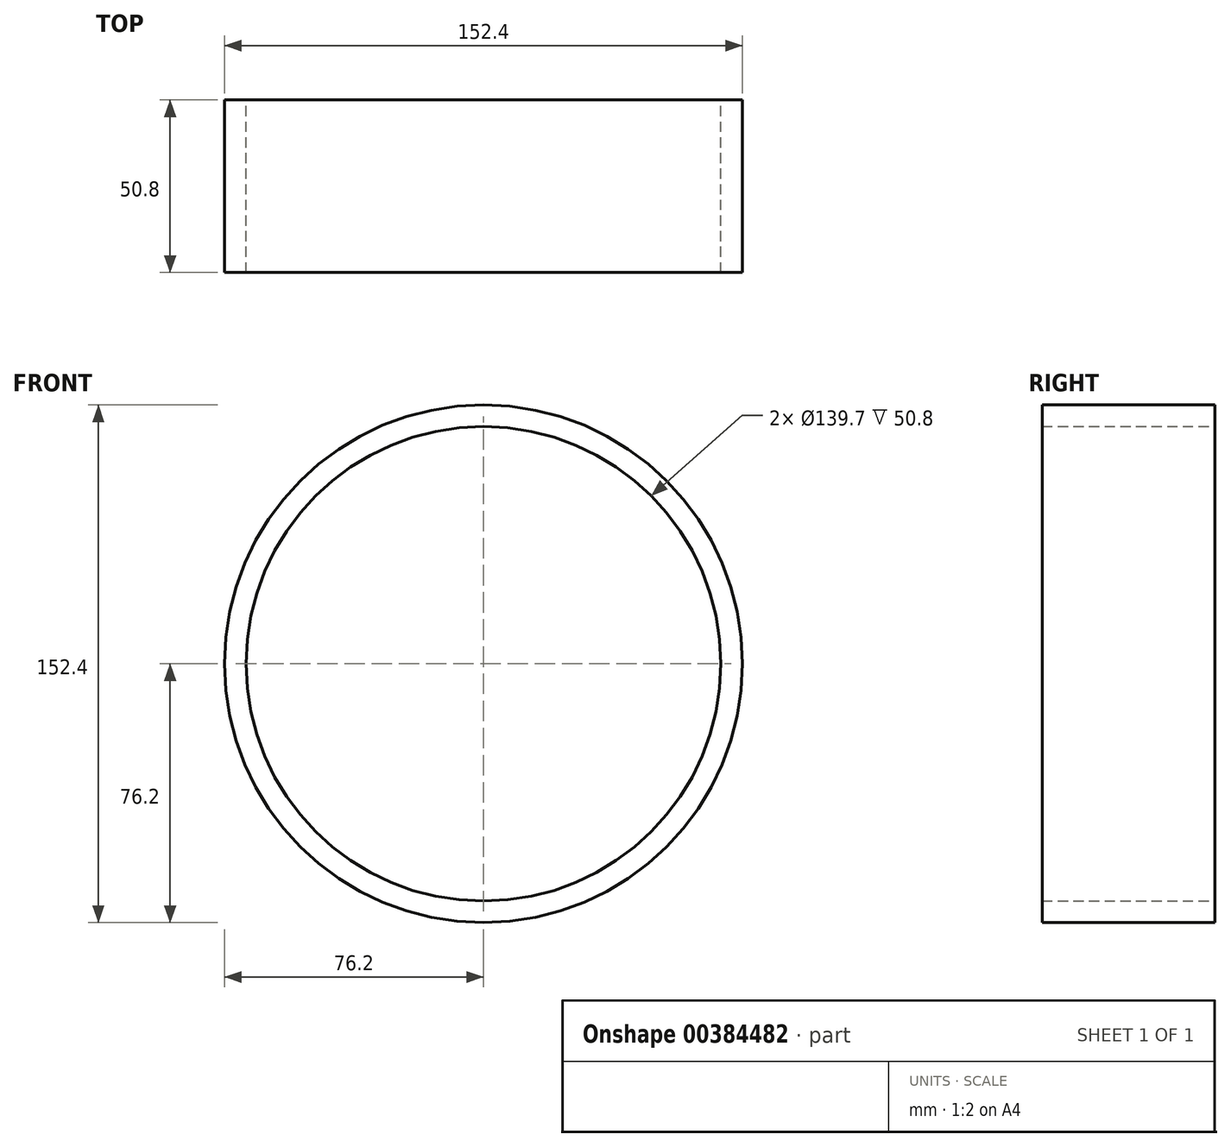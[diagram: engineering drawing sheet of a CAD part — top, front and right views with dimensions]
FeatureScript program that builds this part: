
annotation { "Feature Type Name" : "Feature", "Feature Type Description" : "" }
export const myFeature = defineFeature(function(context is Context, id is Id, definition is map)
    precondition{}
    {
        {
            var Q0;
            Q0=qCreatedBy(makeId("Front.planeOp"),FACE);
            var sketch = newSketch(context, id + "F0", { "sketchPlane" : qUnion([Q0])});
            skCircle(sketch, "E0", {"center": v(0, 0) * mm, "radius": 76.2 * mm});
            skCircle(sketch, "E1", {"center": v(0, 0) * mm, "radius": 69.85 * mm});
            skCircle(sketch, "E2", {"center": v(0, 0) * mm, "radius": 57.15 * mm});
            skSolve(sketch);
        }
        {
            var Q0;
            Q0=makeQuery(id+"F0.imprint","IMPRINT",FACE,{"disambiguationData":[TD([[makeQuery(id+"F0.imprint","IMPRINT",EDGE,{"derivedFrom":sQuery(id+"F0.wireOp",EDGE,"E0")}),1.0]])]});
            extrude(context, id + "F1", {"entities" : qUnion([Q0]), "depth" : 50.8 * mm});
        }
    });
